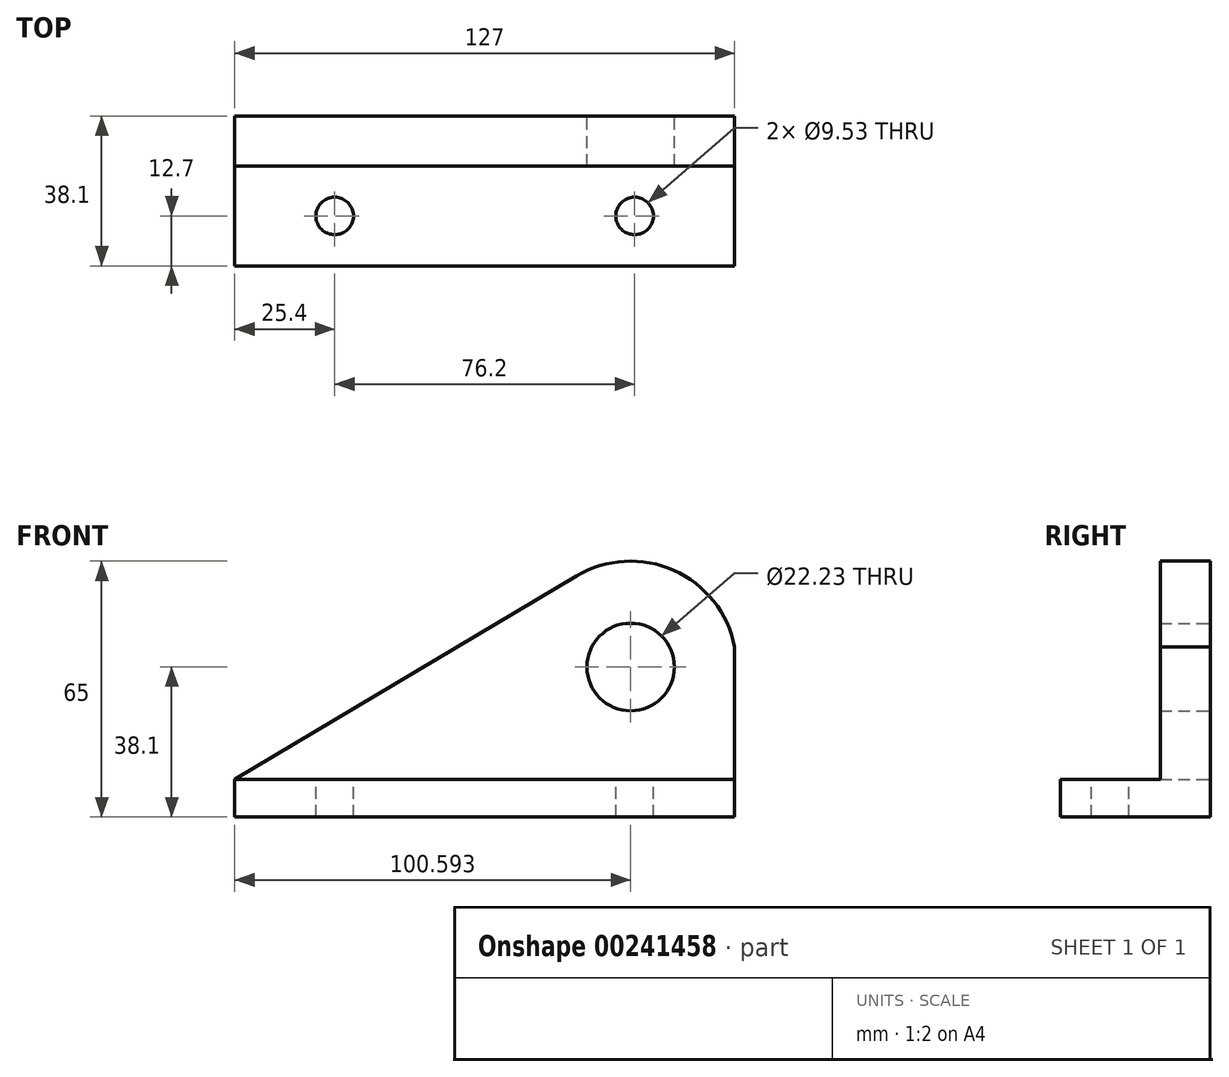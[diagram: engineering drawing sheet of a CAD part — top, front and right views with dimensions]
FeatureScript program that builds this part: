
annotation { "Feature Type Name" : "Feature", "Feature Type Description" : "" }
export const myFeature = defineFeature(function(context is Context, id is Id, definition is map)
    precondition{}
    {
        {
            var Q0;
            Q0=qCreatedBy(makeId("Front.planeOp"),FACE);
            var sketch = newSketch(context, id + "F0", { "sketchPlane" : qUnion([Q0])});
            skLineSegment(sketch, "E0", {"start": v(0, 0) * mm, "end": v(127, 0) * mm});
            skLineSegment(sketch, "E1", {"start": v(127, 0) * mm, "end": v(127, 9.53) * mm});
            skLineSegment(sketch, "E2", {"start": v(127, 9.53) * mm, "end": v(0, 9.53) * mm});
            skLineSegment(sketch, "E3", {"start": v(0, 9.53) * mm, "end": v(0, 0) * mm});
            skLineSegment(sketch, "E4", {"start": v(127, 9.53) * mm, "end": v(127, 43.24) * mm});
            skArc(sketch, "E5", {"start": v(127, 32.96) * mm, "mid": v(116.07, 60.1) * mm, "end": v(86.83, 61.22) * mm});
            skLineSegment(sketch, "E6", {"start": v(0, 9.53) * mm, "end": v(86.83, 61.22) * mm});
            skSolve(sketch);
        }
        {
            var Q0;
            Q0=makeQuery(id+"F0.imprint","IMPRINT",FACE,{"disambiguationData":[TD([[makeQuery(id+"F0.imprint","IMPRINT",EDGE,{"derivedFrom":sQuery(id+"F0.wireOp",EDGE,"E0")}),1.0]])]});
            extrude(context, id + "F1", {"entities" : qUnion([Q0]), "depth" : 38.1 * mm});
        }
        {
            var Q0;
            {var subQ5=sQuery(id+"F0.wireOp",EDGE,"E2");Q0=makeQuery(id+"F0.imprint","IMPRINT",FACE,{"disambiguationData":[TD([[makeQuery(id+"F0.imprint","IMPRINT",EDGE,{"derivedFrom":subQ5}),-1.0]])]});}
            extrude(context, id + "F2", {"entities" : qUnion([Q0]), "operationType" : NewBodyOperationType.ADD, "depth" : 12.7 * mm});
        }
        {
            var Q0;
            Q0=sQuery(id+"F0.wireOp",VERTEX,"E5.center");
            var Q1;
            Q1=makeQuery(id+"F1.opExtrude","SWEPT_BODY",BODY,{"disambiguationData":[OSD([sQuery(id+"F0.wireOp",EDGE,"E0"),sQuery(id+"F0.wireOp",EDGE,"E1"),sQuery(id+"F0.wireOp",EDGE,"E2"),sQuery(id+"F0.wireOp",EDGE,"E3")])]});
            hole(context, id + "F3", {"style" : HoleStyle.C_BORE, "endStyle" : HoleEndStyle.THROUGH, "oppositeDirection" : true, "holeDiameter" : 22.22 * mm, "cBoreDiameter" : 22.22 * mm, "cBoreDepth" : 22.22 * mm, "startFromSketch" : true, "locations" : qUnion([Q0]), "scope" : qUnion([Q1]), "isTappedThrough" : true});
        }
        {
            var Q0;
            Q0=makeQuery(id+"F1.opExtrude","SWEPT_FACE",FACE,{"disambiguationData":[OSD([sQuery(id+"F0.wireOp",EDGE,"E2")])]});
            var sketch = newSketch(context, id + "F4", { "sketchPlane" : qUnion([Q0])});
            skLineSegment(sketch, "E7", {"start": v(0, -25.4) * mm, "end": v(25.4, -25.4) * mm});
            skLineSegment(sketch, "E8", {"start": v(25.4, -25.4) * mm, "end": v(101.6, -25.4) * mm});
            skPoint(sketch, "E8.endSnap0", {"position": v(12.7, -25.4) * mm});
            skLineSegment(sketch, "E9", {"start": v(101.6, -25.4) * mm, "end": v(127, -25.4) * mm});
            skSolve(sketch);
        }
        {
            var Q0;
            Q0=sQuery(id+"F4.wireOp",VERTEX,"E7.end");
            var Q1;
            Q1=makeQuery(id+"F1.opExtrude","SWEPT_BODY",BODY,{"disambiguationData":[OSD([sQuery(id+"F0.wireOp",EDGE,"E0"),sQuery(id+"F0.wireOp",EDGE,"E1"),sQuery(id+"F0.wireOp",EDGE,"E2"),sQuery(id+"F0.wireOp",EDGE,"E3")])]});
            hole(context, id + "F5", {"style" : HoleStyle.C_BORE, "endStyle" : HoleEndStyle.THROUGH, "holeDiameter" : 9.52 * mm, "cBoreDiameter" : 9.52 * mm, "cBoreDepth" : 9.52 * mm, "startFromSketch" : true, "locations" : qUnion([Q0]), "scope" : qUnion([Q1]), "isTappedThrough" : true});
        }
        {
            var Q0;
            Q0=sQuery(id+"F4.wireOp",VERTEX,"E9.start");
            var Q1;
            Q1=makeQuery(id+"F1.opExtrude","SWEPT_BODY",BODY,{"disambiguationData":[OSD([sQuery(id+"F0.wireOp",EDGE,"E0"),sQuery(id+"F0.wireOp",EDGE,"E1"),sQuery(id+"F0.wireOp",EDGE,"E2"),sQuery(id+"F0.wireOp",EDGE,"E3")])]});
            hole(context, id + "F6", {"style" : HoleStyle.C_BORE, "endStyle" : HoleEndStyle.THROUGH, "holeDiameter" : 9.52 * mm, "cBoreDiameter" : 9.52 * mm, "cBoreDepth" : 9.52 * mm, "startFromSketch" : true, "locations" : qUnion([Q0]), "scope" : qUnion([Q1]), "isTappedThrough" : true});
        }
    });
